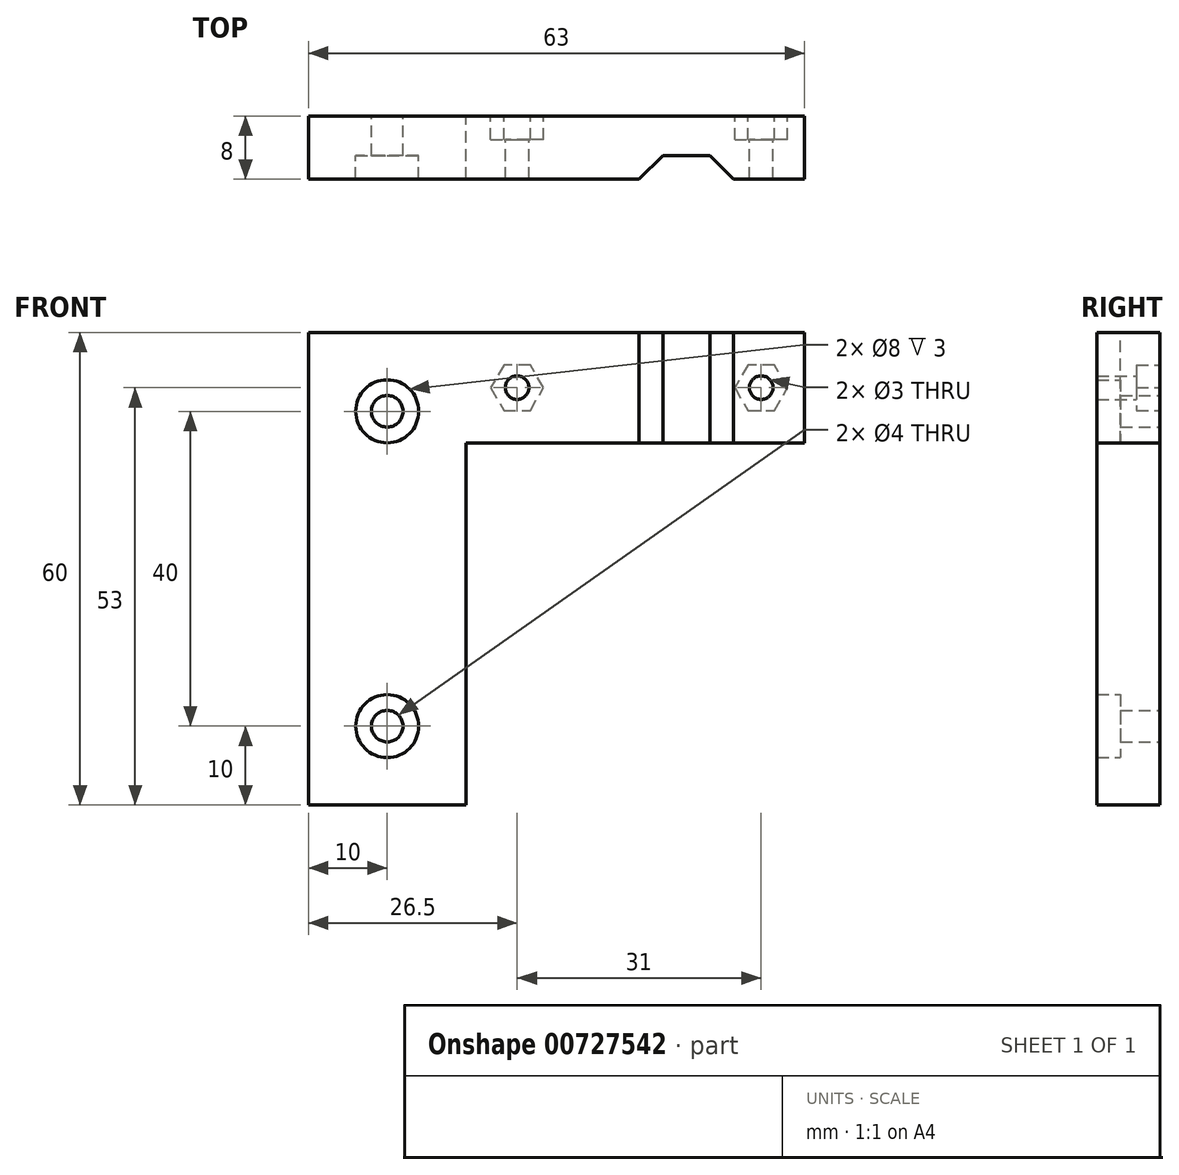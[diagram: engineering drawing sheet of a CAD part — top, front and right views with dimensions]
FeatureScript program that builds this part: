
annotation { "Feature Type Name" : "Feature", "Feature Type Description" : "" }
export const myFeature = defineFeature(function(context is Context, id is Id, definition is map)
    precondition{}
    {
        {
            var Q0;
            Q0=qCreatedBy(makeId("Top.planeOp"),FACE);
            var sketch = newSketch(context, id + "F0", { "sketchPlane" : qUnion([Q0])});
            skLineSegment(sketch, "E0", {"start": v(43, 8) * mm, "end": v(-20, 8) * mm});
            skLineSegment(sketch, "E1", {"start": v(-20, 8) * mm, "end": v(-20, 0) * mm});
            skLineSegment(sketch, "E2", {"start": v(-20, 0) * mm, "end": v(0, 0) * mm});
            skLineSegment(sketch, "E3", {"start": v(0, 0) * mm, "end": v(0, 0) * mm});
            skLineSegment(sketch, "E4", {"start": v(0, 0) * mm, "end": v(22, 0) * mm});
            skLineSegment(sketch, "E5", {"start": v(22, 0) * mm, "end": v(25, 3) * mm});
            skLineSegment(sketch, "E6", {"start": v(25, 3) * mm, "end": v(31, 3) * mm});
            skLineSegment(sketch, "E7", {"start": v(31, 3) * mm, "end": v(34, 0) * mm});
            skLineSegment(sketch, "E8", {"start": v(34, 0) * mm, "end": v(43, 0) * mm});
            skLineSegment(sketch, "E9", {"start": v(43, 0) * mm, "end": v(43, 8) * mm});
            skLineSegment(sketch, "E10", {"start": v(0, 0) * mm, "end": v(0, 8) * mm});
            skSolve(sketch);
        }
        {
            var Q0;
            Q0=makeQuery(id+"F0.imprint","IMPRINT",FACE,{"disambiguationData":[TD([[makeQuery(id+"F0.imprint","IMPRINT",EDGE,{"derivedFrom":sQuery(id+"F0.wireOp",EDGE,"E3")}),1.0]])]});
            var Q1;
            Q1=makeQuery(id+"F0.imprint","IMPRINT",FACE,{"disambiguationData":[TD([[makeQuery(id+"F0.imprint","IMPRINT",EDGE,{"derivedFrom":sQuery(id+"F0.wireOp",EDGE,"E4")}),1.0]])]});
            extrude(context, id + "F1", {"entities" : qUnion([Q0, Q1]), "oppositeDirection" : true, "depth" : 14 * mm, "offsetDistance" : 25 * mm});
        }
        {
            var Q0;
            {var subQ0=sQuery(id+"F0.wireOp",EDGE,"E1");Q0=makeQuery(id+"F0.imprint","IMPRINT",FACE,{"disambiguationData":[TD([[makeQuery(id+"F0.imprint","IMPRINT",EDGE,{"derivedFrom":subQ0}),1.0]])]});}
            extrude(context, id + "F2", {"entities" : qUnion([Q0]), "operationType" : NewBodyOperationType.ADD, "oppositeDirection" : true, "depth" : 60 * mm, "offsetDistance" : 25 * mm});
        }
        {
            var Q0;
            {var subQ0=sQuery(id+"F0.wireOp",EDGE,"E0");Q0=makeQuery(id+"F2.boolean.opBoolean","MERGE",FACE,{"derivedFrom":[makeQuery(id+"F1.opExtrude","SWEPT_FACE",FACE,{"disambiguationData":[OSD([subQ0])]}),makeQuery(id+"F2.opExtrude","SWEPT_FACE",FACE,{"disambiguationData":[OSD([subQ0])]})]});}
            var sketch = newSketch(context, id + "F3", { "sketchPlane" : qUnion([Q0])});
            skCircle(sketch, "E11", {"center": v(-37.5, -7) * mm, "radius": 1.5 * mm});
            skCircle(sketch, "E12", {"center": v(-6.5, -7) * mm, "radius": 1.5 * mm});
            skCircle(sketch, "E13", {"center": v(10, -10) * mm, "radius": 2 * mm});
            skCircle(sketch, "E14", {"center": v(10, -50) * mm, "radius": 2 * mm});
            skCircle(sketch, "E15.cCircle", {"center": v(-37.5, -7) * mm, "radius": 2.9 * mm, "construction": true});
            skLineSegment(sketch, "E15.0", {"start": v(-35.83, -9.9) * mm, "end": v(-39.17, -9.9) * mm});
            skLineSegment(sketch, "E15.1", {"start": v(-39.17, -9.9) * mm, "end": v(-40.85, -7) * mm});
            skLineSegment(sketch, "E15.2", {"start": v(-40.85, -7) * mm, "end": v(-39.17, -4.1) * mm});
            skLineSegment(sketch, "E15.3", {"start": v(-39.17, -4.1) * mm, "end": v(-35.83, -4.1) * mm});
            skLineSegment(sketch, "E15.4", {"start": v(-35.83, -4.1) * mm, "end": v(-34.15, -7) * mm});
            skLineSegment(sketch, "E15.5", {"start": v(-34.15, -7) * mm, "end": v(-35.83, -9.9) * mm});
            skPoint(sketch, "E15.0.midPoint", {"position": v(-37.5, -9.9) * mm});
            skCircle(sketch, "E16.cCircle", {"center": v(-6.5, -7) * mm, "radius": 2.9 * mm, "construction": true});
            skLineSegment(sketch, "E16.0", {"start": v(-4.83, -9.9) * mm, "end": v(-8.17, -9.9) * mm});
            skLineSegment(sketch, "E16.1", {"start": v(-8.17, -9.9) * mm, "end": v(-9.85, -7) * mm});
            skLineSegment(sketch, "E16.2", {"start": v(-9.85, -7) * mm, "end": v(-8.17, -4.1) * mm});
            skLineSegment(sketch, "E16.3", {"start": v(-8.17, -4.1) * mm, "end": v(-4.83, -4.1) * mm});
            skLineSegment(sketch, "E16.4", {"start": v(-4.83, -4.1) * mm, "end": v(-3.15, -7) * mm});
            skLineSegment(sketch, "E16.5", {"start": v(-3.15, -7) * mm, "end": v(-4.83, -9.9) * mm});
            skPoint(sketch, "E16.0.midPoint", {"position": v(-6.5, -9.9) * mm});
            skCircle(sketch, "E17", {"center": v(10, -10) * mm, "radius": 4 * mm});
            skCircle(sketch, "E18", {"center": v(10, -50) * mm, "radius": 4 * mm});
            skCircle(sketch, "E19", {"center": v(-6.5, -7) * mm, "radius": 3.35 * mm, "construction": true});
            skSolve(sketch);
        }
        {
            var Q0;
            Q0=makeQuery(id+"F3.imprint","IMPRINT",FACE,{"disambiguationData":[TD([[makeQuery(id+"F3.imprint","IMPRINT",EDGE,{"derivedFrom":sQuery(id+"F3.wireOp",EDGE,"E11")}),1.0]])]});
            var Q1;
            Q1=makeQuery(id+"F3.imprint","IMPRINT",FACE,{"disambiguationData":[TD([[makeQuery(id+"F3.imprint","IMPRINT",EDGE,{"derivedFrom":sQuery(id+"F3.wireOp",EDGE,"E12")}),1.0]])]});
            var Q2;
            Q2=makeQuery(id+"F3.imprint","IMPRINT",FACE,{"disambiguationData":[TD([[makeQuery(id+"F3.imprint","IMPRINT",EDGE,{"derivedFrom":sQuery(id+"F3.wireOp",EDGE,"E13")}),1.0]])]});
            var Q3;
            Q3=makeQuery(id+"F3.imprint","IMPRINT",FACE,{"disambiguationData":[TD([[makeQuery(id+"F3.imprint","IMPRINT",EDGE,{"derivedFrom":sQuery(id+"F3.wireOp",EDGE,"E14")}),1.0]])]});
            var Q4;
            Q4=makeQuery(id+"F3.imprint","IMPRINT",FACE,{"disambiguationData":[TD([[makeQuery(id+"F3.imprint","IMPRINT",EDGE,{"derivedFrom":sQuery(id+"F3.wireOp",EDGE,"E13")}),-1.0]])]});
            var Q5;
            Q5=makeQuery(id+"F3.imprint","IMPRINT",FACE,{"disambiguationData":[TD([[makeQuery(id+"F3.imprint","IMPRINT",EDGE,{"derivedFrom":sQuery(id+"F3.wireOp",EDGE,"E14")}),-1.0]])]});
            extrude(context, id + "F4", {"entities" : qUnion([Q0, Q1, Q2, Q3, Q4, Q5]), "operationType" : NewBodyOperationType.REMOVE, "endBound" : BoundingType.THROUGH_ALL, "oppositeDirection" : true, "depth" : 25 * mm, "offsetDistance" : 25 * mm});
        }
        {
            var Q0;
            Q0=makeQuery(id+"F3.imprint","IMPRINT",FACE,{"disambiguationData":[TD([[makeQuery(id+"F3.imprint","IMPRINT",EDGE,{"derivedFrom":sQuery(id+"F3.wireOp",EDGE,"E12")}),-1.0]])]});
            var Q1;
            Q1=makeQuery(id+"F3.imprint","IMPRINT",FACE,{"disambiguationData":[TD([[makeQuery(id+"F3.imprint","IMPRINT",EDGE,{"derivedFrom":sQuery(id+"F3.wireOp",EDGE,"E11")}),-1.0]])]});
            extrude(context, id + "F5", {"entities" : qUnion([Q0, Q1]), "operationType" : NewBodyOperationType.REMOVE, "oppositeDirection" : true, "depth" : 3 * mm, "offsetDistance" : 25 * mm});
        }
        {
            var Q0;
            Q0=makeQuery(id+"F3.imprint","IMPRINT",FACE,{"disambiguationData":[TD([[makeQuery(id+"F3.imprint","IMPRINT",EDGE,{"derivedFrom":sQuery(id+"F3.wireOp",EDGE,"E13")}),-1.0]])]});
            var Q1;
            Q1=makeQuery(id+"F3.imprint","IMPRINT",FACE,{"disambiguationData":[TD([[makeQuery(id+"F3.imprint","IMPRINT",EDGE,{"derivedFrom":sQuery(id+"F3.wireOp",EDGE,"E14")}),-1.0]])]});
            extrude(context, id + "F6", {"entities" : qUnion([Q0, Q1]), "operationType" : NewBodyOperationType.ADD, "oppositeDirection" : true, "depth" : 5 * mm, "offsetDistance" : 25 * mm});
        }
    });
